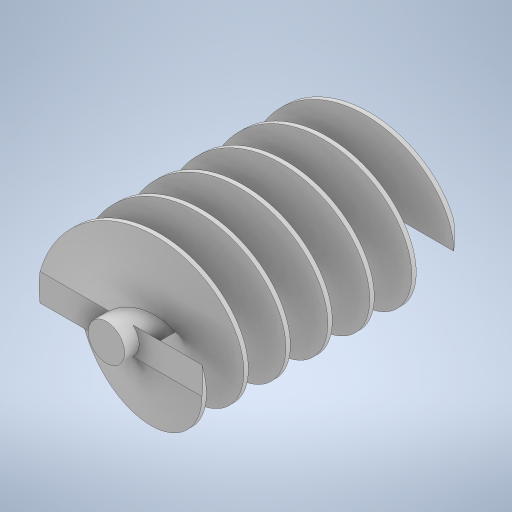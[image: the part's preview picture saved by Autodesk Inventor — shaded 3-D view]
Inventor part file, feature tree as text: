
AUTODESK INVENTOR PART (.ipt)
format: ipt  version: 2023 (Build 270158000, 158)  size: 1,448,448 bytes
history: native  units: in
note: dims shown in document units (in); Inventor stores cm internally (conversion verified against a paired STEP export)
features: extrude x4, sketch x3, other x2, sweep x1
ambient origin geometry x8: Origin, YZ Plane, XZ Plane, XY Plane, X Axis, Y Axis, Z Axis, Center Point
bodies: Solid1 (feature_tree)
feature tree (10):
  sketch  "Sketch1"  dims[d0=1.7717in d1=0.3937in]
  extrude  "Extrusion1"  Depth=0.3937in
  sketch  "Sketch2"  dims[d2=2.7165in d3=0.0in d4=2.7165in d5=1.1811in d6=0.5906in d7=0.0in d10=0.0in d11=0.0in d12=0.0984in d13=0.0984in d14=0.5906in d15=0.0in d18=0.1575in d19=0.0in d20=0.3543in d21=0.0in]
  other  "Work Axis1"
  sketch  "3D Sketch1"
  sweep  "Sweep1"
  extrude  "Extrusion3"  TaperAngle=0.0deg  [1 undecoded]
  extrude  "Extrusion4"  Depth=0.3543in
  extrude  "Extrusion5"  Depth=0.3543in
  other  "Helical Curve1"
note: 1 required parameter value undecoded (feature->parameter linkage not recoverable at this tier; creation-order binding heuristic only, values carry confidence <= 0.55)
